# Revit family: Doors_Vinyl_TD_Outswing_ADA-Friendly-Sill-with-10-Bottom-Rail_Quaker
name_source: partatom
category: Doors
units: mm (PartAtom-declared; Revit-internal decimal feet)

## family parameters
Always vertical = Yes
Classification Number = 23.30.20.00
Cut with Voids When Loaded = No
Host = Wall
Room Calculation Point = No
Shared = No

## types (1)
- 3'-0" x 7'-0"
    Analytic Construction = <None>
    Default Sill Height = 3' - 0"
    Define Thermal Properties by = Schematic Type
    Description = Outswing Door, Vinyl, ADA Friendly Sill with 10" Bott Rail
    Frame Material = Vinyl - Quaker
    Glass Material = Glass - Quaker
    Height = 7' - 0"
    Keynote = 08 15 00
    Manufacturer = Quaker Windows & Doors
    Model = Vinyl TD Outswing
    Offset From Center = 0' - 0"
    Product Page URL = https://www.arcat.com
    URL = https://www.quakerwindows.com
    Wall Closure = By host
    Width = 3' - 0"

## geometry (parser evidence)
native form markers: Sweep x6
no freeform markers — native parametric forms only
